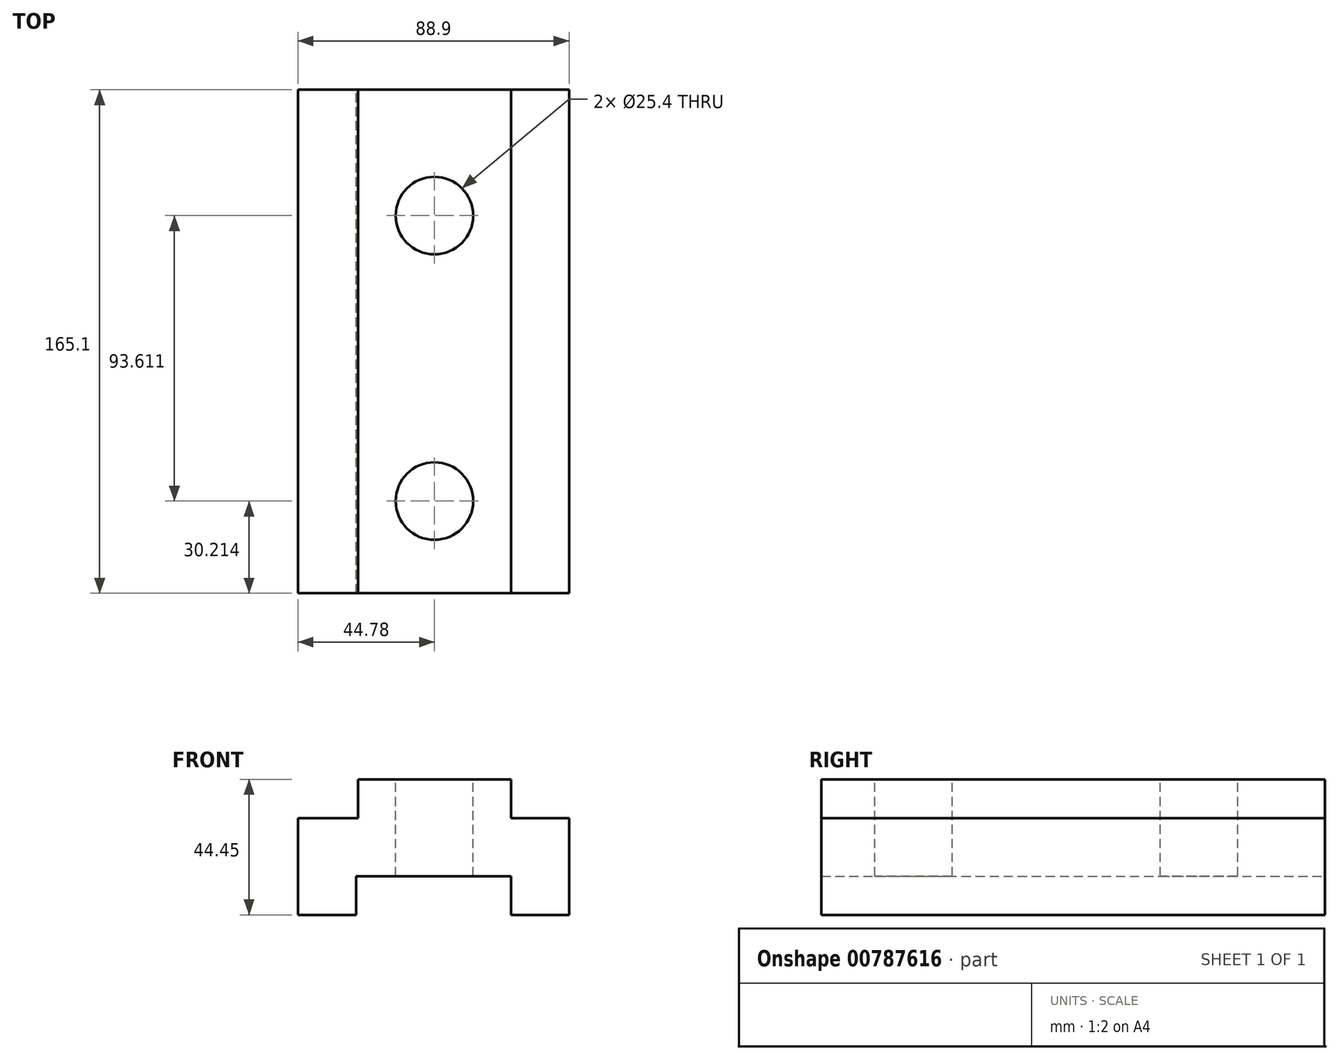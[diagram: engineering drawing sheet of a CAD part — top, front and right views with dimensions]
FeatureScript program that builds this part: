
annotation { "Feature Type Name" : "Feature", "Feature Type Description" : "" }
export const myFeature = defineFeature(function(context is Context, id is Id, definition is map)
    precondition{}
    {
        {
            var Q0;
            Q0=qCreatedBy(makeId("Front.planeOp"),FACE);
            var sketch = newSketch(context, id + "F0", { "sketchPlane" : qUnion([Q0])});
            skLineSegment(sketch, "E0", {"start": v(0, 0) * mm, "end": v(19.05, 0) * mm});
            skLineSegment(sketch, "E1", {"start": v(19.05, 0) * mm, "end": v(19.05, 12.7) * mm});
            skLineSegment(sketch, "E2", {"start": v(19.05, 12.7) * mm, "end": v(69.85, 12.7) * mm});
            skLineSegment(sketch, "E3", {"start": v(69.85, 12.7) * mm, "end": v(69.85, 0) * mm});
            skLineSegment(sketch, "E4", {"start": v(69.85, 0) * mm, "end": v(88.9, 0) * mm});
            skLineSegment(sketch, "E5", {"start": v(88.9, 0) * mm, "end": v(88.9, 31.75) * mm});
            skLineSegment(sketch, "E6", {"start": v(88.9, 31.75) * mm, "end": v(69.85, 31.75) * mm});
            skLineSegment(sketch, "E7", {"start": v(69.85, 31.75) * mm, "end": v(69.85, 44.45) * mm});
            skLineSegment(sketch, "E8", {"start": v(70.5, 44.45) * mm, "end": v(19.7, 44.45) * mm});
            skLineSegment(sketch, "E9", {"start": v(19.7, 44.45) * mm, "end": v(19.7, 31.75) * mm});
            skLineSegment(sketch, "E10", {"start": v(19.7, 31.75) * mm, "end": v(0, 31.75) * mm});
            skLineSegment(sketch, "E11", {"start": v(0, 31.75) * mm, "end": v(0, 0) * mm});
            skSolve(sketch);
        }
        {
            var Q0;
            Q0=makeQuery(id+"F0.imprint","IMPRINT",FACE,{"disambiguationData":[TD([[makeQuery(id+"F0.imprint","IMPRINT",EDGE,{"derivedFrom":sQuery(id+"F0.wireOp",EDGE,"E0")}),1.0]])]});
            extrude(context, id + "F1", {"entities" : qUnion([Q0]), "depth" : 165.1 * mm, "offsetDistance" : 25.4 * mm});
        }
        {
            var Q0;
            Q0=makeQuery(id+"F1.opExtrude","SWEPT_FACE",FACE,{"disambiguationData":[OSD([sQuery(id+"F0.wireOp",EDGE,"E8")])]});
            var sketch = newSketch(context, id + "F2", { "sketchPlane" : qUnion([Q0])});
            skLineSegment(sketch, "E12", {"start": v(44.78, 0) * mm, "end": v(44.78, -41.28) * mm, "construction": true});
            skLineSegment(sketch, "E13", {"start": v(44.78, -41.28) * mm, "end": v(44.78, -134.89) * mm, "construction": true});
            skCircle(sketch, "E14", {"center": v(44.78, -41.28) * mm, "radius": 12.7 * mm});
            skCircle(sketch, "E15", {"center": v(44.78, -134.89) * mm, "radius": 12.7 * mm});
            skSolve(sketch);
        }
        {
            var Q0;
            Q0=makeQuery(id+"F2.imprint","IMPRINT",FACE,{"disambiguationData":[TD([[makeQuery(id+"F2.imprint","IMPRINT",EDGE,{"derivedFrom":sQuery(id+"F2.wireOp",EDGE,"E15")}),1.0]])]});
            var Q1;
            Q1=makeQuery(id+"F2.imprint","IMPRINT",FACE,{"disambiguationData":[TD([[makeQuery(id+"F2.imprint","IMPRINT",EDGE,{"derivedFrom":sQuery(id+"F2.wireOp",EDGE,"E14")}),1.0]])]});
            extrude(context, id + "F3", {"entities" : qUnion([Q0, Q1]), "operationType" : NewBodyOperationType.REMOVE, "oppositeDirection" : true, "depth" : 82.55 * mm, "offsetDistance" : 25.4 * mm});
        }
    });
